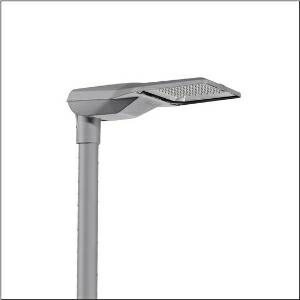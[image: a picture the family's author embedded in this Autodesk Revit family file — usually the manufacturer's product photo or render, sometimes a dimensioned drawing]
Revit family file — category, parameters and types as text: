
# Revit family: streetlight_sl_21_iq_midi___st1_0a_5xe3d21d08nb_d513
name_source: partatom
category: Lighting Fixtures
units: mm (PartAtom-declared; Revit-internal decimal feet)

## family parameters
Cut with Voids When Loaded = No
Host = Face
Light Source = No
Part Type = Normal
Room Calculation Point = No
Round Connector Dimension = Use Diameter
Shared = No

## types (1)
- --- (1 x LED, 19210 lm, 155.5 W, 2200K)
    Apparent Load = 155 VA
    CIE Flux Codes = 40 73 97 100 100
    Color Rendering = 70
    Color Temperature = 2200K
    Default Elevation = 1800 mm
    Description = Streetlight SL 21 iQ midi, mast luminaire, primary light control with lens, of PMMA, primary optical cover: cover, of toughened safety glass, transparent, light distribution: ST1.0a, light emission: direct distribution, primary light characteristic: asymmetric, installation type: post-top, side-entry, LED, High Power LED, rated luminous flux: 19.210lm, luminous efficacy: 124lm/W, light colour: 722, colour temperature: 2200K, control gear: iQ-Comfort, control: Auto-Match, Temp-Guard, Lumen-Switch, Night-Set, Smart-Wire, Light-Fading, Desk-Remote (wireless, voltage-free reading and setting of iQ features in the workshop via application-optimized NFC function/RFID function), optimised constant luminous flux control (CLO 2.0), pre-setting: linear dimming characteristic, mains connection: 230..240V, AC, 50/60Hz, start of lifetime: 156W, end of service life: 162W, reduction: 69W, luminaire housing, of diecast aluminium, powder-coated, SITECO metallic grey (DB 702S), corrosivity category C5 high according to DIN EN ISO 12944, please order mast flange separately, inclination adjustable: 0°, 5°, 10°, 15°, sealing non-destructively replaceable, multi-level sealing system, length: 644mm, width: 335mm, height: 110mm, mast flange for spigot size: 42mm (side-entry): 5XC10008XM4, 60/48mm (side-entry/post-top): 5XC10108XM2, 76/60mm (side-entry/post-top): 5XC10108XM1, mounting height: 4..8m, protection rating (complete): IP66, insulation class (complete): insulation class II (safety insulation), certification: CE, ENEC, ENEC+, VDE, impact resistance: IK10, permissible operating ambient temperature for outdoor applications: -40..+50°C, standard-compliant lighting for roads and squares, packaging unit: 1 piece

Light Distribution: ST1.0a
    Height = 111 mm
    Lamp = 1 x LED
    Lamp Light Flux = 19210 lm
    Lamp Power = 155.5 W
    Lamp count = 1
    Length = 644 mm
    Luminous efficacy = 124 lm/W
    Manufacturer = Siteco
    ModVariant = No
    Model = 5XE3D21D08NB
    Number of Poles = 1
    OnlyDefault = Yes
    Power Factor = 1
    Product Name = Streetlight SL 21 iQ midi | ST1.0a
    Product group = mast luminaire | pylon top
    ProductGroupID = 6100
    Protection Class = Protection class II
    Protection Degree = IP 66
    RLX_Detail_Level = 1
    RLX_Emergency_Light_Flux = 0 lm
    RLX_Emergency_Type = 0
    RLX_Emergency_Type_DB = No
    RlxData = <blob elided: 27245 chars, md5=f755b7fe>
    Socket = socket
    Standby Power = 0 W
    System Light Flux = 19210 lm
    System Power = 155 W
    Type Comments = factory setting: luminous flux: 100 % | dim-lin: 254 | 823 mA
    Type Image = l_1004298.jpg
    URL = http://relux.com
    VarID = @adj_170447
    Voltage = 0 V
    Weight = 0.00 kg
    Width = 336 mm

## geometry (parser evidence)
native form markers: Blend x4, Sweep x9
no freeform markers — native parametric forms only
